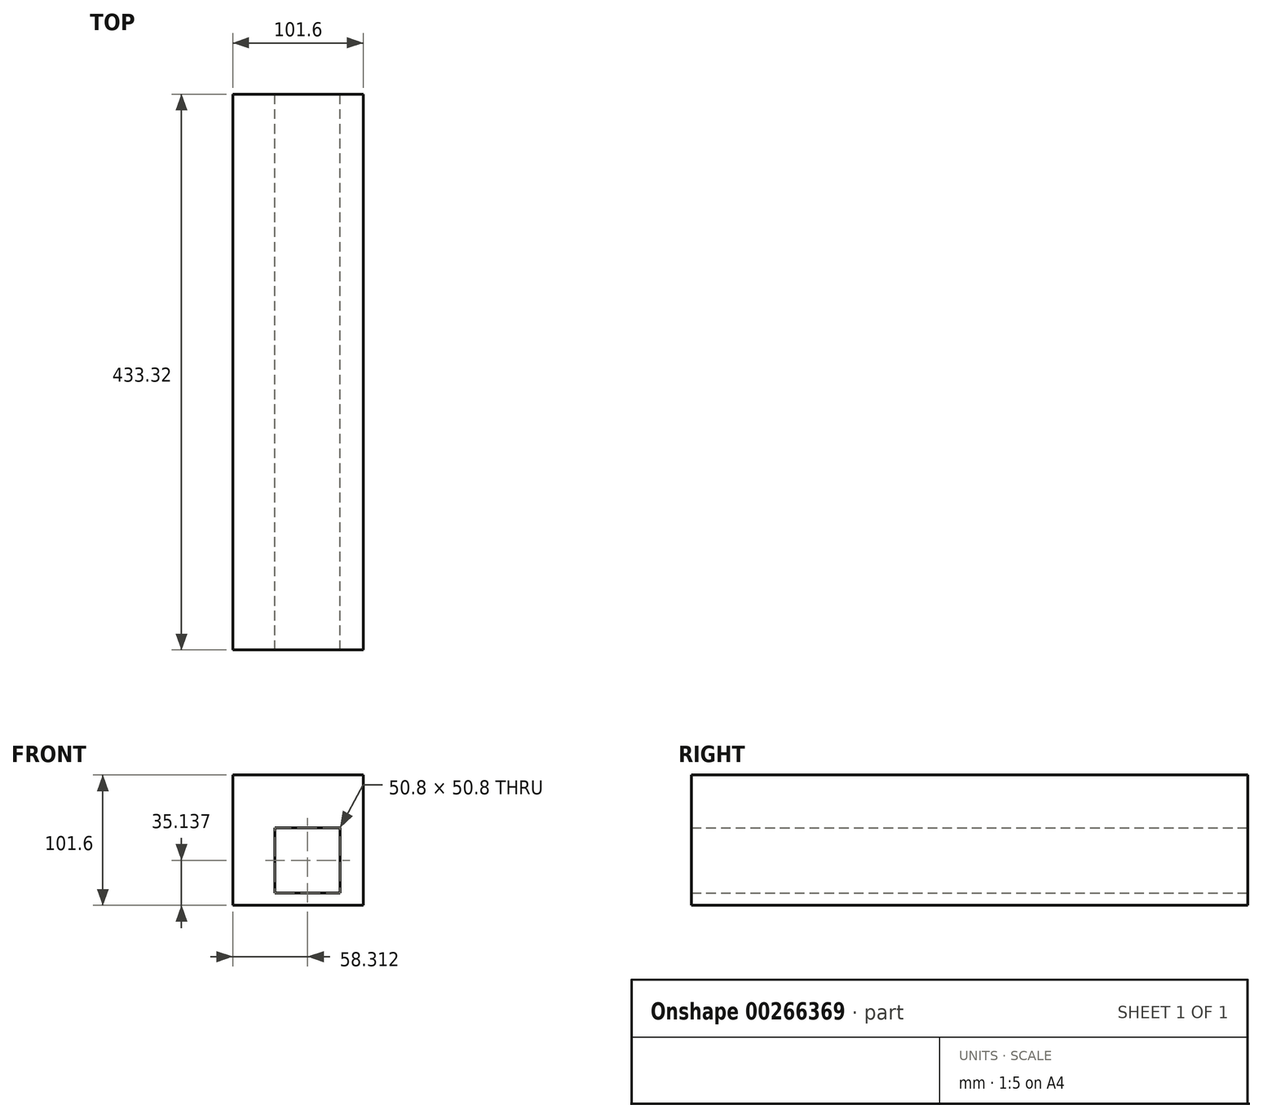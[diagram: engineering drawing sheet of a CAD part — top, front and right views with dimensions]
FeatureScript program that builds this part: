
annotation { "Feature Type Name" : "Feature", "Feature Type Description" : "" }
export const myFeature = defineFeature(function(context is Context, id is Id, definition is map)
    precondition{}
    {
        {
            var Q0;
            Q0=qCreatedBy(makeId("Front.planeOp"),FACE);
            var sketch = newSketch(context, id + "F0", { "sketchPlane" : qUnion([Q0])});
            skLineSegment(sketch, "E0.bottom", {"start": v(-0.52, -9.93) * mm, "end": v(50.28, -9.93) * mm});
            skLineSegment(sketch, "E0.top", {"start": v(-0.52, -60.73) * mm, "end": v(50.28, -60.73) * mm});
            skLineSegment(sketch, "E0.left", {"start": v(-0.52, -9.93) * mm, "end": v(-0.52, -60.73) * mm});
            skLineSegment(sketch, "E0.right", {"start": v(50.28, -9.93) * mm, "end": v(50.28, -60.73) * mm});
            skLineSegment(sketch, "E1.bottom", {"start": v(-33.43, 31.13) * mm, "end": v(68.17, 31.13) * mm});
            skLineSegment(sketch, "E1.top", {"start": v(-33.43, -70.47) * mm, "end": v(68.17, -70.47) * mm});
            skLineSegment(sketch, "E1.left", {"start": v(-33.43, 31.13) * mm, "end": v(-33.43, -70.47) * mm});
            skLineSegment(sketch, "E1.right", {"start": v(68.17, 31.13) * mm, "end": v(68.17, -70.47) * mm});
            skSolve(sketch);
        }
        {
            var Q0;
            Q0=makeQuery(id+"F0.imprint","IMPRINT",FACE,{"disambiguationData":[TD([[makeQuery(id+"F0.imprint","IMPRINT",EDGE,{"derivedFrom":sQuery(id+"F0.wireOp",EDGE,"E0.bottom")}),1.0]])]});
            extrude(context, id + "F1", {"entities" : qUnion([Q0]), "depth" : 433.32 * mm});
        }
    });
